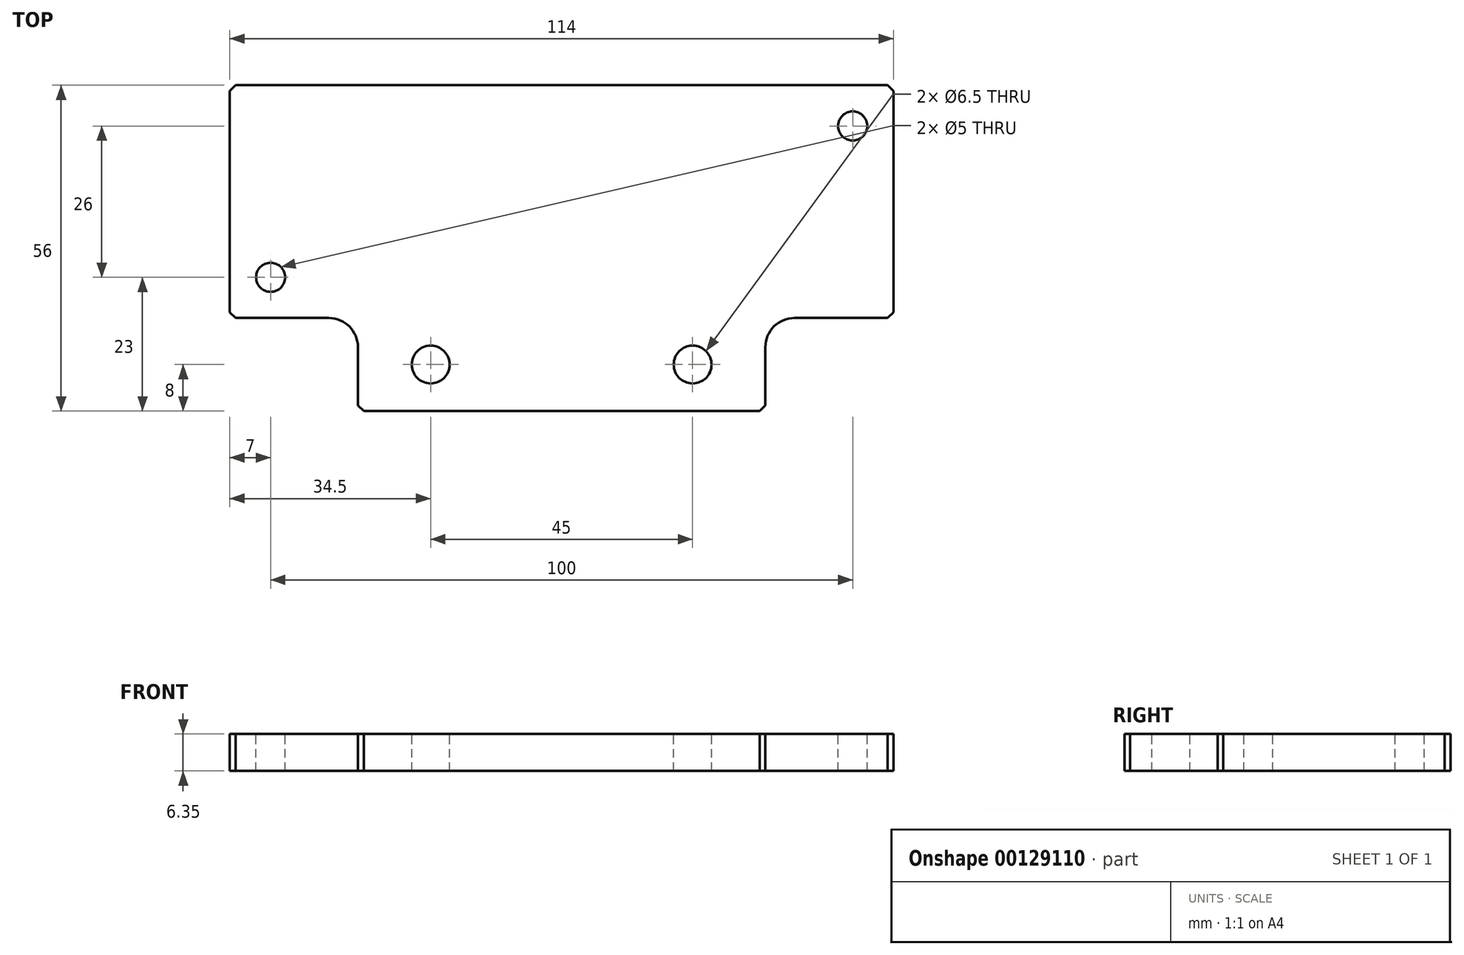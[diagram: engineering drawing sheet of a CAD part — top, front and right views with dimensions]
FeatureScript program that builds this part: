
annotation { "Feature Type Name" : "Feature", "Feature Type Description" : "" }
export const myFeature = defineFeature(function(context is Context, id is Id, definition is map)
    precondition{}
    {
        {
            var Q0;
            Q0=qCreatedBy(makeId("Top.planeOp"),FACE);
            var sketch = newSketch(context, id + "F0", { "sketchPlane" : qUnion([Q0])});
            skLineSegment(sketch, "E0.0", {"start": v(57, 20) * mm, "end": v(-57, 20) * mm});
            skLineSegment(sketch, "E1.0", {"start": v(57, 20) * mm, "end": v(57, -20) * mm});
            skLineSegment(sketch, "E1.1", {"start": v(-57, 20) * mm, "end": v(-57, -20) * mm});
            skLineSegment(sketch, "E2", {"start": v(0, 0) * mm, "end": v(57, 0) * mm, "construction": true});
            skLineSegment(sketch, "E3", {"start": v(0, 0) * mm, "end": v(0, -36) * mm, "construction": true});
            skLineSegment(sketch, "E4.MirrorCS", {"start": v(0, 0) * mm, "end": v(0, 20) * mm, "construction": true});
            skCircle(sketch, "E5.MirrorC", {"center": v(-50, -13) * mm, "radius": 3.3 * mm, "construction": true});
            skCircle(sketch, "E6.MirrorC", {"center": v(50, 13) * mm, "radius": 3.3 * mm, "construction": true});
            skLineSegment(sketch, "E7.0", {"start": v(35, -36) * mm, "end": v(-35, -36) * mm});
            skPoint(sketch, "E8.orphan", {"position": v(0, -20) * mm});
            skPoint(sketch, "E9.orphan", {"position": v(57, -20) * mm});
            skLineSegment(sketch, "E10", {"start": v(35, -36) * mm, "end": v(35, -25) * mm});
            skLineSegment(sketch, "E11", {"start": v(40, -20) * mm, "end": v(57, -20) * mm});
            skCircle(sketch, "E12", {"center": v(22.5, -28) * mm, "radius": 3.25 * mm});
            skCircle(sketch, "E13.MirrorC", {"center": v(-22.5, -28) * mm, "radius": 3.25 * mm});
            skLineSegment(sketch, "E14.MirrorCS", {"start": v(-35, -36) * mm, "end": v(-35, -25) * mm});
            skLineSegment(sketch, "E15.MirrorCS", {"start": v(-40, -20) * mm, "end": v(-57, -20) * mm});
            skPoint(sketch, "E16.visualSharp", {"position": v(-35, -20) * mm});
            skArc(sketch, "E16.filletArc", {"start": v(-35, -25) * mm, "mid": v(-36.46, -21.46) * mm, "end": v(-40, -20) * mm});
            skPoint(sketch, "E17.visualSharp", {"position": v(35, -20) * mm});
            skArc(sketch, "E17.filletArc", {"start": v(40, -20) * mm, "mid": v(36.46, -21.46) * mm, "end": v(35, -25) * mm});
            skCircle(sketch, "E18", {"center": v(0, -28) * mm, "radius": 4 * mm, "construction": true});
            skCircle(sketch, "E19.MirrorC", {"center": v(-50, 13) * mm, "radius": 3.3 * mm, "construction": true});
            skCircle(sketch, "E20.MirrorC", {"center": v(50, -13) * mm, "radius": 3.3 * mm, "construction": true});
            skLineSegment(sketch, "E21", {"start": v(-40, -20) * mm, "end": v(40, -20) * mm, "construction": true});
            skSolve(sketch);
        }
        {
            var Q0;
            Q0 = qSketchRegion(id + "F0", true);
            extrude(context, id + "F1", {"entities" : qUnion([Q0]), "oppositeDirection" : true, "depth" : 6.35 * mm});
        }
        {
            var Q0;
            Q0=makeQuery(id+"F1.opExtrude","SWEPT_EDGE",EDGE,{"disambiguationData":[OSD([sQuery(id+"F0.wireOp",EDGE,"E7.0"),sQuery(id+"F0.wireOp",EDGE,"E14.MirrorCS")])]});
            var Q1;
            Q1=makeQuery(id+"F1.opExtrude","SWEPT_EDGE",EDGE,{"disambiguationData":[OSD([sQuery(id+"F0.wireOp",EDGE,"E1.1"),sQuery(id+"F0.wireOp",EDGE,"E15.MirrorCS")])]});
            var Q2;
            Q2=makeQuery(id+"F1.opExtrude","SWEPT_EDGE",EDGE,{"disambiguationData":[OSD([sQuery(id+"F0.wireOp",EDGE,"E7.0"),sQuery(id+"F0.wireOp",EDGE,"E10")])]});
            var Q3;
            Q3=makeQuery(id+"F1.opExtrude","SWEPT_EDGE",EDGE,{"disambiguationData":[OSD([sQuery(id+"F0.wireOp",EDGE,"E1.0"),sQuery(id+"F0.wireOp",EDGE,"E11")])]});
            var Q4;
            Q4=makeQuery(id+"F1.opExtrude","SWEPT_EDGE",EDGE,{"disambiguationData":[OSD([sQuery(id+"F0.wireOp",EDGE,"E0.0"),sQuery(id+"F0.wireOp",EDGE,"E1.1")])]});
            var Q5;
            Q5=makeQuery(id+"F1.opExtrude","SWEPT_EDGE",EDGE,{"disambiguationData":[OSD([sQuery(id+"F0.wireOp",EDGE,"E0.0"),sQuery(id+"F0.wireOp",EDGE,"E1.0")])]});
            chamfer(context, id + "F2", {"entities" : qUnion([Q0, Q1, Q2, Q3, Q4, Q5]), "width" : 1 * mm, "tangentPropagation" : true});
        }
        {
            var Q0;
            Q0=sQuery(id+"F0.wireOp",VERTEX,"E5.MirrorC.center");
            var Q1;
            Q1=sQuery(id+"F0.wireOp",VERTEX,"E6.MirrorC.center");
            var Q2;
            Q2=makeQuery(id+"F1.opExtrude","SWEPT_BODY",BODY,{"disambiguationData":[OSD([sQuery(id+"F0.wireOp",EDGE,"E0.0"),sQuery(id+"F0.wireOp",EDGE,"E1.0"),sQuery(id+"F0.wireOp",EDGE,"E1.1"),sQuery(id+"F0.wireOp",EDGE,"E7.0"),sQuery(id+"F0.wireOp",EDGE,"E10"),sQuery(id+"F0.wireOp",EDGE,"E11"),sQuery(id+"F0.wireOp",EDGE,"E12"),sQuery(id+"F0.wireOp",EDGE,"E13.MirrorC"),sQuery(id+"F0.wireOp",EDGE,"E14.MirrorCS"),sQuery(id+"F0.wireOp",EDGE,"E15.MirrorCS"),sQuery(id+"F0.wireOp",EDGE,"E16.filletArc"),sQuery(id+"F0.wireOp",EDGE,"E17.filletArc"),sQuery(id+"F0.wireOp",EDGE,"E18")])]});
            hole(context, id + "F3", {"style" : HoleStyle.SIMPLE, "endStyle" : HoleEndStyle.THROUGH, "standardTappedOrClearance" : lookupTablePath({ "standard" : "ISO", "engagement" : "75%", "pitch" : "1 mm", "size" : "M6", "type" : "Tapped" }), "standardBlindInLast" : lookupTablePath({ "standard" : "ISO", "engagement" : "75%", "pitch" : "1 mm", "size" : "M6", "type" : "Tapped" }), "holeDiameter" : 5 * mm, "startFromSketch" : true, "locations" : qUnion([Q0, Q1]), "scope" : qUnion([Q2]), "isTappedThrough" : true, "majorDiameter" : 6 * mm, "showTappedDepth" : true});
        }
    });
